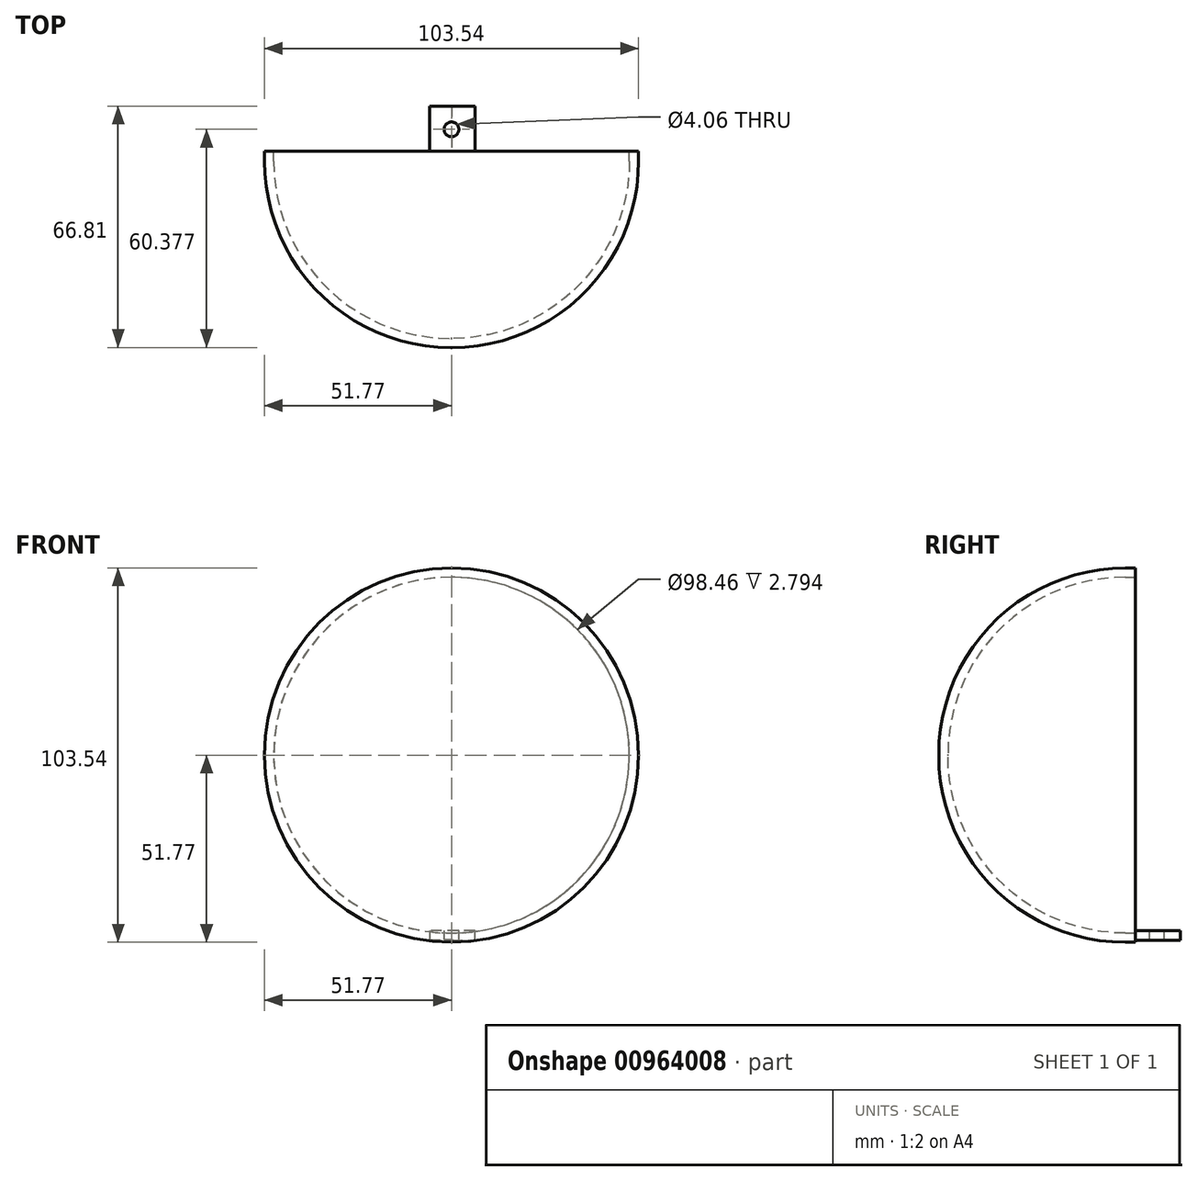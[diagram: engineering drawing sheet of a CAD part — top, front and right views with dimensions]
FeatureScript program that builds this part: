
annotation { "Feature Type Name" : "Feature", "Feature Type Description" : "" }
export const myFeature = defineFeature(function(context is Context, id is Id, definition is map)
    precondition{}
    {
        {
            var Q0;
            Q0=qCreatedBy(makeId("Front.planeOp"),FACE);
            var sketch = newSketch(context, id + "F0", { "sketchPlane" : qUnion([Q0])});
            skCircle(sketch, "E0", {"center": v(0, 0) * mm, "radius": 51.77 * mm});
            skSolve(sketch);
        }
        {
            var Q0;
            Q0 = qSketchRegion(id + "F0", true);
            extrude(context, id + "F1", {"entities" : qUnion([Q0]), "depth" : 54.36 * mm, "offsetDistance" : 25.4 * mm});
        }
        {
            var Q0;
            Q0=makeQuery(id+"F1.opExtrude","CAP_EDGE",EDGE,{"disambiguationData":[OSD([sQuery(id+"F0.wireOp",EDGE,"E0")])],"isStart":false});
            fillet(context, id + "F2", {"entities" : qUnion([Q0]), "radius" : 51.56 * mm, "tangentPropagation" : true, "allowEdgeOverflow" : false});
        }
        {
            var Q0;
            Q0=makeQuery(id+"F1.opExtrude","CAP_FACE",FACE,{"disambiguationData":[OSD([sQuery(id+"F0.wireOp",EDGE,"E0")])],"isStart":true});
            shell(context, id + "F3", {"entities" : qUnion([Q0]), "thickness" : 2.54 * mm});
        }
        {
            var Q0;
            Q0=qCreatedBy(makeId("Front.planeOp"),FACE);
            var sketch = newSketch(context, id + "F4", { "sketchPlane" : qUnion([Q0])});
            skLineSegment(sketch, "E1", {"start": v(6.47, -51.27) * mm, "end": v(6.47, -48.52) * mm});
            skLineSegment(sketch, "E2", {"start": v(6.47, -48.52) * mm, "end": v(-6.1, -48.52) * mm});
            skLineSegment(sketch, "E3", {"start": v(-6.1, -48.52) * mm, "end": v(-6.1, -51.14) * mm});
            skLineSegment(sketch, "E4", {"start": v(-6.1, -51.14) * mm, "end": v(0, -51.14) * mm});
            skLineSegment(sketch, "E5", {"start": v(0, -51.14) * mm, "end": v(6.47, -51.27) * mm});
            skSolve(sketch);
        }
        {
            var Q0;
            Q0=makeQuery(id+"F4.imprint","IMPRINT",FACE,{"disambiguationData":[TD([[makeQuery(id+"F4.imprint","IMPRINT",EDGE,{"derivedFrom":sQuery(id+"F4.wireOp",EDGE,"E1")}),1.0]])]});
            extrude(context, id + "F5", {"entities" : qUnion([Q0]), "operationType" : NewBodyOperationType.ADD, "oppositeDirection" : true, "depth" : 12.45 * mm, "offsetDistance" : 25.4 * mm});
        }
        {
            var Q0;
            Q0=makeQuery(id+"F5.opExtrude","SWEPT_FACE",FACE,{"disambiguationData":[OSD([sQuery(id+"F4.wireOp",EDGE,"E2")])]});
            var sketch = newSketch(context, id + "F6", { "sketchPlane" : qUnion([Q0])});
            skCircle(sketch, "E6", {"center": v(0, 6.02) * mm, "radius": 2.28 * mm});
            skSolve(sketch);
        }
        {
            var Q0;
            Q0=sQuery(id+"F6.wireOp",VERTEX,"E6.center");
            var Q1;
            Q1=makeQuery(id+"F1.opExtrude","SWEPT_BODY",BODY,{"disambiguationData":[OSD([sQuery(id+"F0.wireOp",EDGE,"E0")])]});
            hole(context, id + "F7", {"style" : HoleStyle.C_BORE, "endStyle" : HoleEndStyle.THROUGH, "holeDiameter" : 2.54 * mm, "cBoreDiameter" : 4.06 * mm, "cBoreDepth" : 6.35 * mm, "majorDiameter" : 6.35 * mm, "isTappedThrough" : true, "tappedDepth" : 12.7 * mm, "tapClearance" : 3, "locations" : qUnion([Q0]), "scope" : qUnion([Q1])});
        }
    });
